# Revit family: PARLÉ TCM-1 Network Box_rev2
name_source: partatom
category: Communication Devices
units: mm (PartAtom-declared; Revit-internal decimal feet)

## family parameters
Cut with Voids When Loaded = No
Host = Face
Maintain Annotation Orientation = No
Part Type = Normal
Room Calculation Point = Yes
Round Connector Dimension = Use Diameter
Shared = Yes

## types (3) — shared parameters
Case Finish = Black Finish
Default Elevation = 0' - 0"
Height = 0' - 2"
Manufacturer = Biamp Systems
Manufacturer URL = https://www.biamp.com
Product Documentation Link = https://downloads.biamp.com
Product Page URL = https://www.biamp.com
Regulatory Compliance = FCC Part 15B (USA) CE marked (Europe) UL and C-UL listed (USA and Canada) RoHS Directive (Europe) Evaluated to the requirements of UL 2043 and is suitable for use in air handling spaces

## per-type parameters (varying)
| type | Amplifier | Connector | Depth | Description | Max Distance Between Devices | Model | POE Power | POE+ | Power | TCM-1EX | TCM1/1A | Weight Product | Width |
| PARLÉ™ TCM-1 - Plenum Network Box | None | Two RJ-45: one between TCM-1 plenum box and switch, the other between TCM-1 plenum box and additional TCM-1EX plenum box; 2-pin 3.5 mm Phoenix connector to TCM-1 microphone | 0' - 7 1/8" | Pendant Microphone Network Box only. Refer to Parle TCM-1 Mic for additional data. | 330 feet (100 meters) from switch to TCM-1 plenum box; 33 feet (10 meters) for daisy-chained connections between TCM plenum boxes | PARLÉ™ TCM-1 | 15.4 | No | PoE (IEEE 802.3at Class 3, 15.4W) | No | Yes | 2.4 | 0' - 7" |
| PARLÉ™ TCM-1A - Plenum Network Box | 2X Class D - 4Ω (per channel): 40W - 8Ω (per channel): 30W | Two RJ-45: one between TCM-1 plenum box and switch, the other between TCM-1 plenum box and additional TCM-1EX plenum box; 2-pin 3.5 mm Phoenix connector to TCM-1 microphone | 0' - 7 1/8" | Pendant Microphone Network Box with amplifier only. Refer to Parle TCM-1 Mic for additional data. | 330 feet (100 meters) from switch to TCM-1 plenum box; 33 feet (10 meters) for daisy-chained connections between TCM plenum boxes | PARLÉ™ TCM-1A | 30 | Yes | PoE (IEEE 802.3at Class 3, 30W) | No | Yes | 2.4 | 0' - 7" |
| PARLÉ™ TCM-1EX - Plenum Network Box | None | Two RJ-45: one between TCM-1EX plenum box and TCM-1 or TCM-1A, the other between TCM-1EX plenum box and additional TCM-1EX plenum box; 2-pin 3.5 mm Phoenix connector to TCM-1EX microphone | 0' - 5 1/4" | Pendant Microphone Expansion Mic only. Requires TCM 1/1A. | 33 feet (10 meters) between TCM plenum boxes | PARLÉ™ TCM-1EX | 0 | No | Custom/Proprietary | Yes | No | 0.8 | 0' - 4" |

## geometry (parser evidence)
native form markers: Sweep x3
no freeform markers — native parametric forms only
